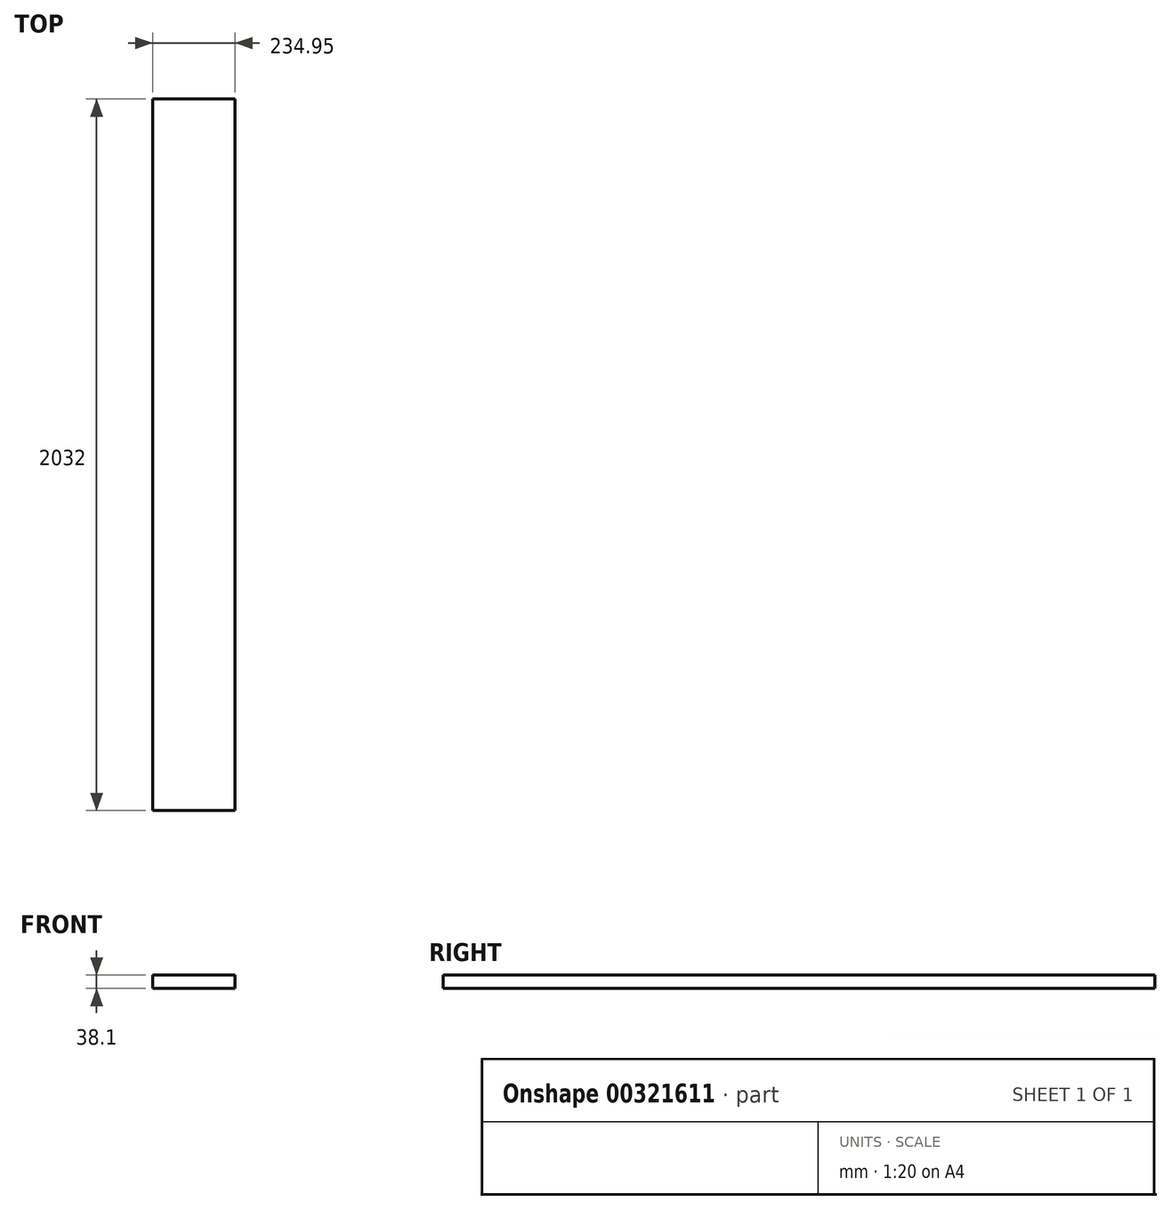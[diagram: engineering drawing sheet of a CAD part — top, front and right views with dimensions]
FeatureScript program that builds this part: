
annotation { "Feature Type Name" : "Feature", "Feature Type Description" : "" }
export const myFeature = defineFeature(function(context is Context, id is Id, definition is map)
    precondition{}
    {
        {
            var Q0;
            Q0=qCreatedBy(makeId("Front.planeOp"),FACE);
            var sketch = newSketch(context, id + "F0", { "sketchPlane" : qUnion([Q0])});
            skLineSegment(sketch, "E0.bottom", {"start": v(-51.35, 25.43) * mm, "end": v(183.6, 25.43) * mm});
            skLineSegment(sketch, "E0.top", {"start": v(-51.35, -12.67) * mm, "end": v(183.6, -12.67) * mm});
            skLineSegment(sketch, "E0.left", {"start": v(-51.35, 25.43) * mm, "end": v(-51.35, -12.67) * mm});
            skLineSegment(sketch, "E0.right", {"start": v(183.6, 25.43) * mm, "end": v(183.6, -12.67) * mm});
            skSolve(sketch);
        }
        {
            var Q0;
            Q0=makeQuery(id+"F0.imprint","IMPRINT",FACE,{"disambiguationData":[TD([[makeQuery(id+"F0.imprint","IMPRINT",EDGE,{"derivedFrom":sQuery(id+"F0.wireOp",EDGE,"E0.bottom")}),-1.0]])]});
            extrude(context, id + "F1", {"entities" : qUnion([Q0]), "depth" : 2032 * mm});
        }
    });
